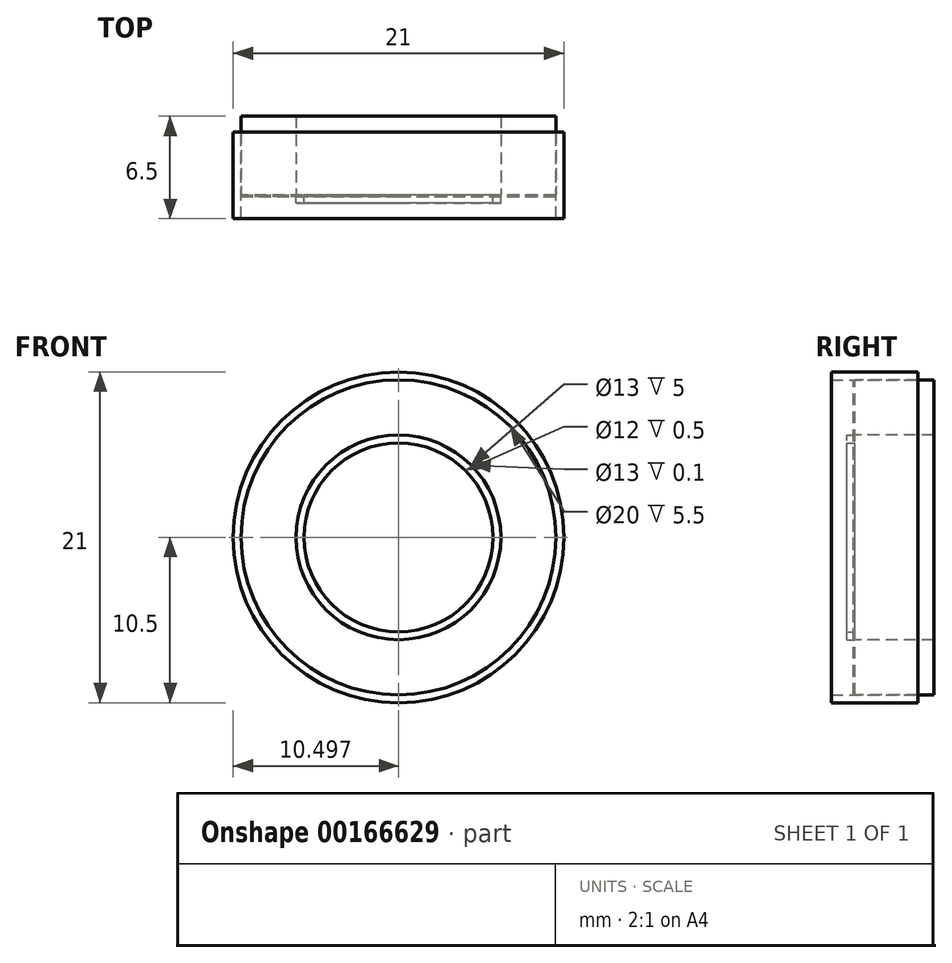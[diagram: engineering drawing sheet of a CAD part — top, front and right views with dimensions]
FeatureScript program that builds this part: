
annotation { "Feature Type Name" : "Feature", "Feature Type Description" : "" }
export const myFeature = defineFeature(function(context is Context, id is Id, definition is map)
    precondition{}
    {
        {
            var Q0;
            Q0=qCreatedBy(makeId("Front.planeOp"),FACE);
            var sketch = newSketch(context, id + "F0", { "sketchPlane" : qUnion([Q0])});
            skCircle(sketch, "E0", {"center": v(-128.68, -12.32) * mm, "radius": 10.5 * mm});
            skCircle(sketch, "E1", {"center": v(-128.68, -12.32) * mm, "radius": 10 * mm});
            skCircle(sketch, "E2", {"center": v(-128.68, -12.32) * mm, "radius": 6.5 * mm});
            skCircle(sketch, "E3", {"center": v(-128.68, -12.32) * mm, "radius": 6 * mm});
            skSolve(sketch);
        }
        {
            var Q0;
            Q0=makeQuery(id+"F0.imprint","IMPRINT",FACE,{"disambiguationData":[TD([[makeQuery(id+"F0.imprint","IMPRINT",EDGE,{"derivedFrom":sQuery(id+"F0.wireOp",EDGE,"E0")}),1.0]])]});
            extrude(context, id + "F1", {"entities" : qUnion([Q0]), "depth" : 1.5 * mm, "hasSecondDirection" : true, "secondDirectionOppositeDirection" : true, "secondDirectionDepth" : 4 * mm});
        }
        {
            var Q0;
            Q0=makeQuery(id+"F0.imprint","IMPRINT",FACE,{"disambiguationData":[TD([[makeQuery(id+"F0.imprint","IMPRINT",EDGE,{"derivedFrom":sQuery(id+"F0.wireOp",EDGE,"E2")}),1.0]])]});
            extrude(context, id + "F2", {"entities" : qUnion([Q0]), "depth" : 0.5 * mm});
        }
        {
            var Q0;
            Q0=makeQuery(id+"F0.imprint","IMPRINT",FACE,{"disambiguationData":[TD([[makeQuery(id+"F0.imprint","IMPRINT",EDGE,{"derivedFrom":sQuery(id+"F0.wireOp",EDGE,"E1")}),1.0]])]});
            extrude(context, id + "F3", {"entities" : qUnion([Q0]), "depth" : .1 * mm});
        }
        {
            var Q0;
            Q0=makeQuery(id+"F0.imprint","IMPRINT",FACE,{"disambiguationData":[TD([[makeQuery(id+"F0.imprint","IMPRINT",EDGE,{"derivedFrom":sQuery(id+"F0.wireOp",EDGE,"E1")}),1.0]])]});
            extrude(context, id + "F4", {"entities" : qUnion([Q0]), "oppositeDirection" : true, "depth" : 5 * mm});
        }
    });
